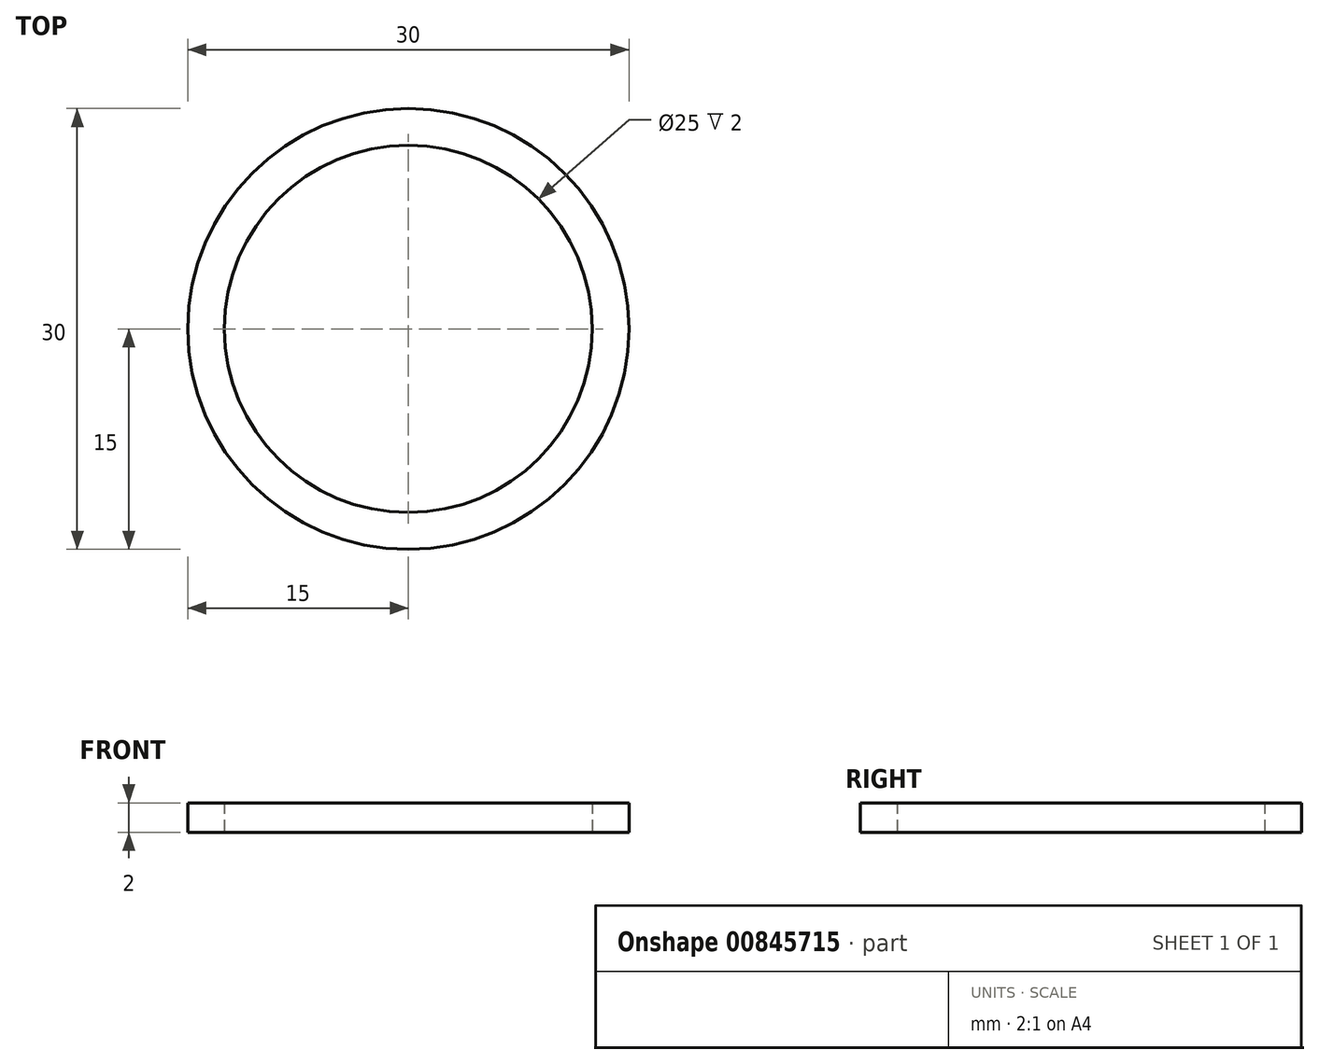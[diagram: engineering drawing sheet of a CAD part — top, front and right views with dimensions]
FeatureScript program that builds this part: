
annotation { "Feature Type Name" : "Feature", "Feature Type Description" : "" }
export const myFeature = defineFeature(function(context is Context, id is Id, definition is map)
    precondition{}
    {
        {
            var Q0;
            Q0=qCreatedBy(makeId("Top.planeOp"),FACE);
            var sketch = newSketch(context, id + "F0", { "sketchPlane" : qUnion([Q0])});
            skCircle(sketch, "E0", {"center": v(0, 0) * mm, "radius": 15 * mm});
            skCircle(sketch, "E1", {"center": v(0, 0) * mm, "radius": 12.5 * mm});
            skSolve(sketch);
        }
        {
            var Q0;
            Q0 = qSketchRegion(id + "F0", true);
            extrude(context, id + "F1", {"entities" : qUnion([Q0]), "depth" : 2 * mm, "offsetDistance" : 25 * mm});
        }
    });
